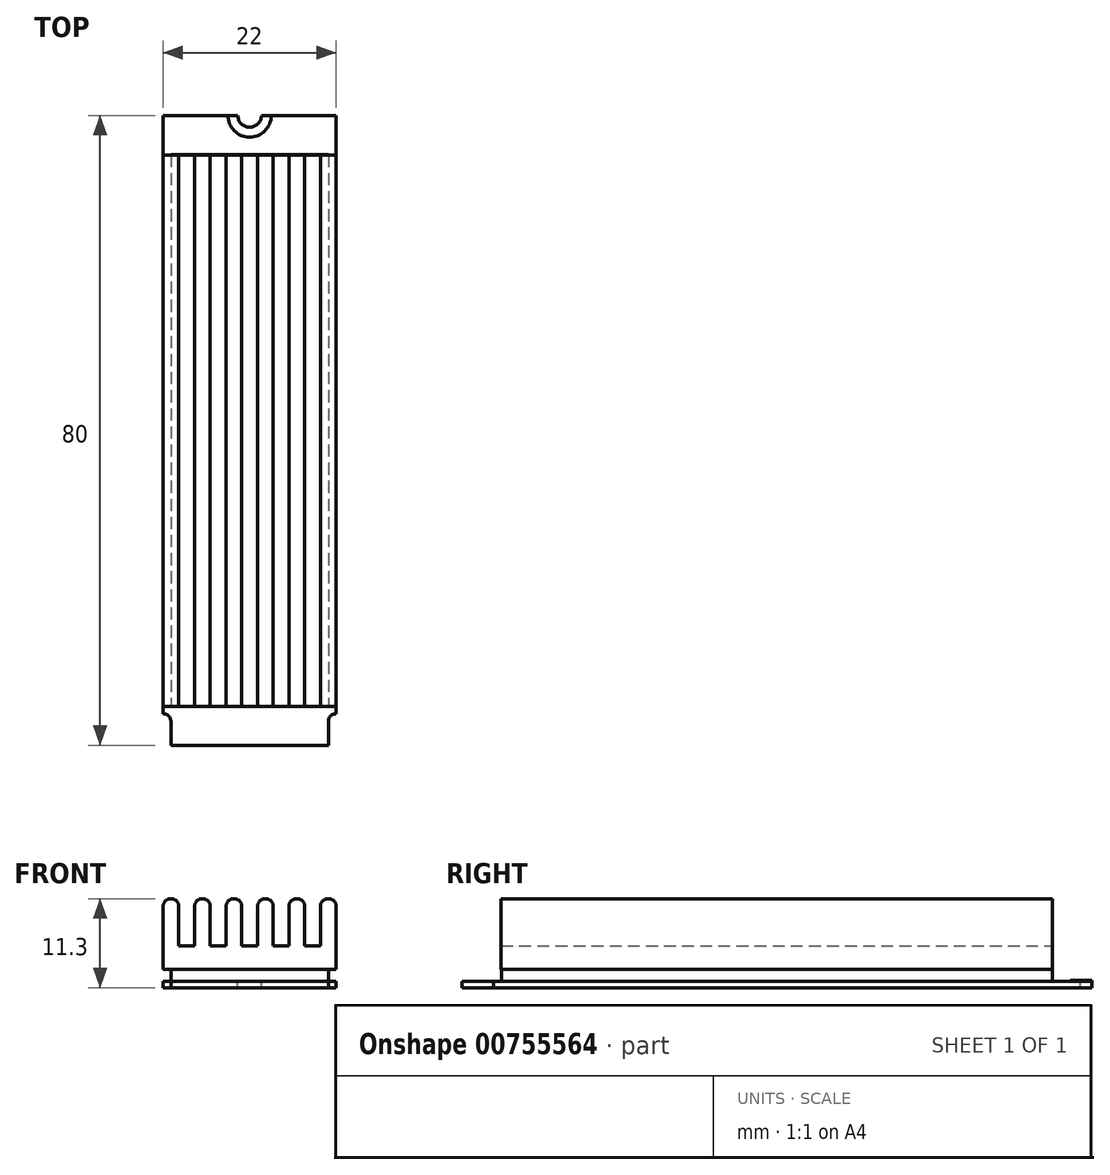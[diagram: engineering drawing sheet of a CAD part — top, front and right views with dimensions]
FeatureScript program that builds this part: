
annotation { "Feature Type Name" : "Feature", "Feature Type Description" : "" }
export const myFeature = defineFeature(function(context is Context, id is Id, definition is map)
    precondition{}
    {
        {
            var Q0;
            Q0=qCreatedBy(makeId("Top.planeOp"),FACE);
            var sketch = newSketch(context, id + "F0", { "sketchPlane" : qUnion([Q0])});
            skLineSegment(sketch, "E0.bottom", {"start": v(-11.32, 40.05) * mm, "end": v(10.68, 40.05) * mm});
            skLineSegment(sketch, "E0.top", {"start": v(-11.32, -35.95) * mm, "end": v(-10.32, -35.95) * mm});
            skLineSegment(sketch, "E0.left", {"start": v(-11.32, 40.05) * mm, "end": v(-11.32, -35.95) * mm});
            skLineSegment(sketch, "E0.right", {"start": v(10.68, 40.05) * mm, "end": v(10.68, -35.95) * mm});
            skLineSegment(sketch, "E1", {"start": v(-10.32, -35.95) * mm, "end": v(-10.32, -39.95) * mm});
            skLineSegment(sketch, "E2", {"start": v(9.68, -39.95) * mm, "end": v(-10.32, -39.95) * mm});
            skLineSegment(sketch, "E3", {"start": v(9.68, -39.95) * mm, "end": v(9.68, -35.95) * mm});
            skLineSegment(sketch, "E4.trimOffspring", {"start": v(9.68, -35.95) * mm, "end": v(10.68, -35.95) * mm});
            skSolve(sketch);
        }
        {
            var Q0;
            Q0=makeQuery(id+"F0.imprint","IMPRINT",FACE,{"disambiguationData":[TD([[makeQuery(id+"F0.imprint","IMPRINT",EDGE,{"derivedFrom":sQuery(id+"F0.wireOp",EDGE,"E0.bottom")}),-1.0]])]});
            extrude(context, id + "F1", {"entities" : qUnion([Q0]), "depth" : .8 * mm, "offsetDistance" : 25 * mm});
        }
        {
            var Q0;
            Q0=makeQuery(id+"F1.opExtrude","SWEPT_EDGE",EDGE,{"disambiguationData":[OSD([sQuery(id+"F0.wireOp",EDGE,"E3"),sQuery(id+"F0.wireOp",EDGE,"E4.trimOffspring")])]});
            var Q1;
            Q1=makeQuery(id+"F1.opExtrude","SWEPT_EDGE",EDGE,{"disambiguationData":[OSD([sQuery(id+"F0.wireOp",EDGE,"E0.top"),sQuery(id+"F0.wireOp",EDGE,"E1")])]});
            fillet(context, id + "F2", {"entities" : qUnion([Q0, Q1]), "radius" : 1 * mm, "tangentPropagation" : true, "allowEdgeOverflow" : false});
        }
        {
            var Q0;
            Q0=makeQuery(id+"F1.opExtrude","CAP_FACE",FACE,{"disambiguationData":[OSD([sQuery(id+"F0.wireOp",EDGE,"E0.bottom"),sQuery(id+"F0.wireOp",EDGE,"E0.top"),sQuery(id+"F0.wireOp",EDGE,"E0.left"),sQuery(id+"F0.wireOp",EDGE,"E0.right"),sQuery(id+"F0.wireOp",EDGE,"E1"),sQuery(id+"F0.wireOp",EDGE,"E2"),sQuery(id+"F0.wireOp",EDGE,"E3"),sQuery(id+"F0.wireOp",EDGE,"E4.trimOffspring")])],"isStart":false});
            var sketch = newSketch(context, id + "F3", { "sketchPlane" : qUnion([Q0])});
            skLineSegment(sketch, "E5.bottom", {"start": v(-10.32, 35.05) * mm, "end": v(9.68, 35.05) * mm});
            skLineSegment(sketch, "E5.top", {"start": v(-10.32, -34.95) * mm, "end": v(9.68, -34.95) * mm});
            skLineSegment(sketch, "E5.left", {"start": v(-10.32, 35.05) * mm, "end": v(-10.32, -34.95) * mm});
            skLineSegment(sketch, "E5.right", {"start": v(9.68, 35.05) * mm, "end": v(9.68, -34.95) * mm});
            skSolve(sketch);
        }
        {
            var Q0;
            Q0=makeQuery(id+"F3.imprint","IMPRINT",FACE,{"disambiguationData":[TD([[makeQuery(id+"F3.imprint","IMPRINT",EDGE,{"derivedFrom":sQuery(id+"F3.wireOp",EDGE,"E5.bottom")}),-1.0]])]});
            extrude(context, id + "F4", {"entities" : qUnion([Q0]), "operationType" : NewBodyOperationType.ADD, "depth" : 1.5 * mm, "offsetDistance" : 25 * mm});
        }
        {
            var Q0;
            Q0=makeQuery(id+"F1.opExtrude","CAP_FACE",FACE,{"disambiguationData":[OSD([sQuery(id+"F0.wireOp",EDGE,"E0.bottom"),sQuery(id+"F0.wireOp",EDGE,"E0.top"),sQuery(id+"F0.wireOp",EDGE,"E0.left"),sQuery(id+"F0.wireOp",EDGE,"E0.right"),sQuery(id+"F0.wireOp",EDGE,"E1"),sQuery(id+"F0.wireOp",EDGE,"E2"),sQuery(id+"F0.wireOp",EDGE,"E3"),sQuery(id+"F0.wireOp",EDGE,"E4.trimOffspring")])],"isStart":false});
            var sketch = newSketch(context, id + "F5", { "sketchPlane" : qUnion([Q0])});
            skCircle(sketch, "E6", {"center": v(-0.32, 40.05) * mm, "radius": 1.5 * mm});
            skCircle(sketch, "E7", {"center": v(-0.32, 40.05) * mm, "radius": 2.75 * mm});
            skSolve(sketch);
        }
        {
            var Q0;
            {var subQ0=sQuery(id+"F5.wireOp",EDGE,"E6");var subQ1=makeQuery(id+"F1.opExtrude","CAP_EDGE",EDGE,{"disambiguationData":[OSD([sQuery(id+"F0.wireOp",EDGE,"E0.bottom")])],"isStart":false});var subQ2=makeQuery(id+"F5.imprint","INTERSECT",VERTEX,{"disambiguationData":[OD(0.0)],"derivedFrom":[subQ1,subQ0]});Q0=makeQuery(id+"F5.imprint","IMPRINT",FACE,{"disambiguationData":[TD([[makeQuery(id+"F5.imprint","IMPRINT",EDGE,{"disambiguationData":[TD([[subQ2,-1.0]])],"derivedFrom":subQ0}),1.0]])]});}
            extrude(context, id + "F6", {"entities" : qUnion([Q0]), "operationType" : NewBodyOperationType.REMOVE, "endBound" : BoundingType.THROUGH_ALL, "oppositeDirection" : true, "depth" : -1 * mm, "offsetDistance" : 25 * mm});
        }
        {
            var Q0;
            {var subQ0=sQuery(id+"F5.wireOp",EDGE,"E6");var subQ1=makeQuery(id+"F1.opExtrude","CAP_EDGE",EDGE,{"disambiguationData":[OSD([sQuery(id+"F0.wireOp",EDGE,"E0.bottom")])],"isStart":false});var subQ2=makeQuery(id+"F5.imprint","INTERSECT",VERTEX,{"disambiguationData":[OD(0.0)],"derivedFrom":[subQ1,subQ0]});Q0=makeQuery(id+"F5.imprint","IMPRINT",FACE,{"disambiguationData":[TD([[makeQuery(id+"F5.imprint","IMPRINT",EDGE,{"disambiguationData":[TD([[subQ2,-1.0]])],"derivedFrom":subQ0}),-1.0]])]});}
            extrude(context, id + "F7", {"entities" : qUnion([Q0]), "operationType" : NewBodyOperationType.ADD, "depth" : .1 * mm, "offsetDistance" : 25 * mm});
        }
        {
            var Q0;
            Q0=qCreatedBy(makeId("Front.planeOp"),FACE);
            var sketch = newSketch(context, id + "F8", { "sketchPlane" : qUnion([Q0])});
            skLineSegment(sketch, "E8", {"start": v(-11.32, 2.3) * mm, "end": v(10.68, 2.3) * mm});
            skLineSegment(sketch, "E9", {"start": v(-11.32, 2.3) * mm, "end": v(-11.32, 11.3) * mm});
            skLineSegment(sketch, "E10", {"start": v(-11.32, 11.3) * mm, "end": v(10.68, 11.3) * mm, "construction": true});
            skLineSegment(sketch, "E11", {"start": v(10.68, 11.3) * mm, "end": v(10.68, 2.3) * mm});
            skLineSegment(sketch, "E12", {"start": v(-11.32, 5.3) * mm, "end": v(10.68, 5.3) * mm});
            skLineSegment(sketch, "E13", {"start": v(-9.32, 11.3) * mm, "end": v(-9.32, 5.3) * mm});
            skLineSegment(sketch, "E14", {"start": v(-7.32, 11.3) * mm, "end": v(-7.32, 5.3) * mm});
            skLineSegment(sketch, "E15", {"start": v(-5.32, 11.3) * mm, "end": v(-5.32, 5.3) * mm});
            skLineSegment(sketch, "E16", {"start": v(-3.32, 11.3) * mm, "end": v(-3.32, 5.3) * mm});
            skLineSegment(sketch, "E17", {"start": v(-1.32, 11.3) * mm, "end": v(-1.32, 5.3) * mm});
            skLineSegment(sketch, "E18", {"start": v(0.68, 11.3) * mm, "end": v(0.68, 5.3) * mm});
            skLineSegment(sketch, "E19", {"start": v(2.68, 11.3) * mm, "end": v(2.68, 5.3) * mm});
            skLineSegment(sketch, "E20", {"start": v(4.68, 11.3) * mm, "end": v(4.68, 5.3) * mm});
            skLineSegment(sketch, "E21", {"start": v(6.68, 11.3) * mm, "end": v(6.68, 5.3) * mm});
            skLineSegment(sketch, "E22", {"start": v(8.68, 11.3) * mm, "end": v(8.68, 5.3) * mm});
            skLineSegment(sketch, "E23", {"start": v(-11.32, 11.3) * mm, "end": v(-9.32, 11.3) * mm});
            skLineSegment(sketch, "E24", {"start": v(-7.32, 11.3) * mm, "end": v(-5.32, 11.3) * mm});
            skLineSegment(sketch, "E25", {"start": v(-3.32, 11.3) * mm, "end": v(-1.32, 11.3) * mm});
            skLineSegment(sketch, "E26", {"start": v(0.68, 11.3) * mm, "end": v(2.68, 11.3) * mm});
            skLineSegment(sketch, "E27", {"start": v(4.68, 11.3) * mm, "end": v(6.68, 11.3) * mm});
            skLineSegment(sketch, "E28", {"start": v(8.68, 11.3) * mm, "end": v(10.68, 11.3) * mm});
            skLineSegment(sketch, "E29", {"start": v(-11.32, 3.3) * mm, "end": v(-10.32, 3.3) * mm});
            skLineSegment(sketch, "E30", {"start": v(-10.32, 3.3) * mm, "end": v(-10.32, 5.3) * mm});
            skLineSegment(sketch, "E31", {"start": v(10.68, 3.3) * mm, "end": v(9.68, 3.3) * mm});
            skLineSegment(sketch, "E32", {"start": v(9.68, 3.3) * mm, "end": v(9.68, 5.3) * mm});
            skSolve(sketch);
        }
        {
            var Q0;
            Q0 = qSketchRegion(id + "F8", true);
            extrude(context, id + "F9", {"entities" : qUnion([Q0]), "endBound" : BoundingType.SYMMETRIC, "depth" : 70 * mm, "offsetDistance" : 25 * mm});
        }
        {
            var Q0;
            Q0=makeQuery(id+"F9.opExtrude","SWEPT_EDGE",EDGE,{"disambiguationData":[OSD([sQuery(id+"F8.wireOp",EDGE,"E9"),sQuery(id+"F8.wireOp",EDGE,"E23")])]});
            var Q1;
            Q1=makeQuery(id+"F9.opExtrude","SWEPT_EDGE",EDGE,{"disambiguationData":[OSD([sQuery(id+"F8.wireOp",EDGE,"E13"),sQuery(id+"F8.wireOp",EDGE,"E23")])]});
            var Q2;
            Q2=makeQuery(id+"F9.opExtrude","SWEPT_EDGE",EDGE,{"disambiguationData":[OSD([sQuery(id+"F8.wireOp",EDGE,"E14"),sQuery(id+"F8.wireOp",EDGE,"E24")])]});
            var Q3;
            Q3=makeQuery(id+"F9.opExtrude","SWEPT_EDGE",EDGE,{"disambiguationData":[OSD([sQuery(id+"F8.wireOp",EDGE,"E15"),sQuery(id+"F8.wireOp",EDGE,"E24")])]});
            var Q4;
            Q4=makeQuery(id+"F9.opExtrude","SWEPT_EDGE",EDGE,{"disambiguationData":[OSD([sQuery(id+"F8.wireOp",EDGE,"E16"),sQuery(id+"F8.wireOp",EDGE,"E25")])]});
            var Q5;
            Q5=makeQuery(id+"F9.opExtrude","SWEPT_EDGE",EDGE,{"disambiguationData":[OSD([sQuery(id+"F8.wireOp",EDGE,"E17"),sQuery(id+"F8.wireOp",EDGE,"E25")])]});
            var Q6;
            Q6=makeQuery(id+"F9.opExtrude","SWEPT_EDGE",EDGE,{"disambiguationData":[OSD([sQuery(id+"F8.wireOp",EDGE,"E18"),sQuery(id+"F8.wireOp",EDGE,"E26")])]});
            var Q7;
            Q7=makeQuery(id+"F9.opExtrude","SWEPT_EDGE",EDGE,{"disambiguationData":[OSD([sQuery(id+"F8.wireOp",EDGE,"E19"),sQuery(id+"F8.wireOp",EDGE,"E26")])]});
            var Q8;
            Q8=makeQuery(id+"F9.opExtrude","SWEPT_EDGE",EDGE,{"disambiguationData":[OSD([sQuery(id+"F8.wireOp",EDGE,"E20"),sQuery(id+"F8.wireOp",EDGE,"E27")])]});
            var Q9;
            Q9=makeQuery(id+"F9.opExtrude","SWEPT_EDGE",EDGE,{"disambiguationData":[OSD([sQuery(id+"F8.wireOp",EDGE,"E21"),sQuery(id+"F8.wireOp",EDGE,"E27")])]});
            var Q10;
            Q10=makeQuery(id+"F9.opExtrude","SWEPT_EDGE",EDGE,{"disambiguationData":[OSD([sQuery(id+"F8.wireOp",EDGE,"E22"),sQuery(id+"F8.wireOp",EDGE,"E28")])]});
            var Q11;
            Q11=makeQuery(id+"F9.opExtrude","SWEPT_EDGE",EDGE,{"disambiguationData":[OSD([sQuery(id+"F8.wireOp",EDGE,"E11"),sQuery(id+"F8.wireOp",EDGE,"E28")])]});
            fillet(context, id + "F10", {"entities" : qUnion([Q0, Q1, Q2, Q3, Q4, Q5, Q6, Q7, Q8, Q9, Q10, Q11]), "radius" : 1 * mm, "tangentPropagation" : true, "allowEdgeOverflow" : false});
        }
    });
